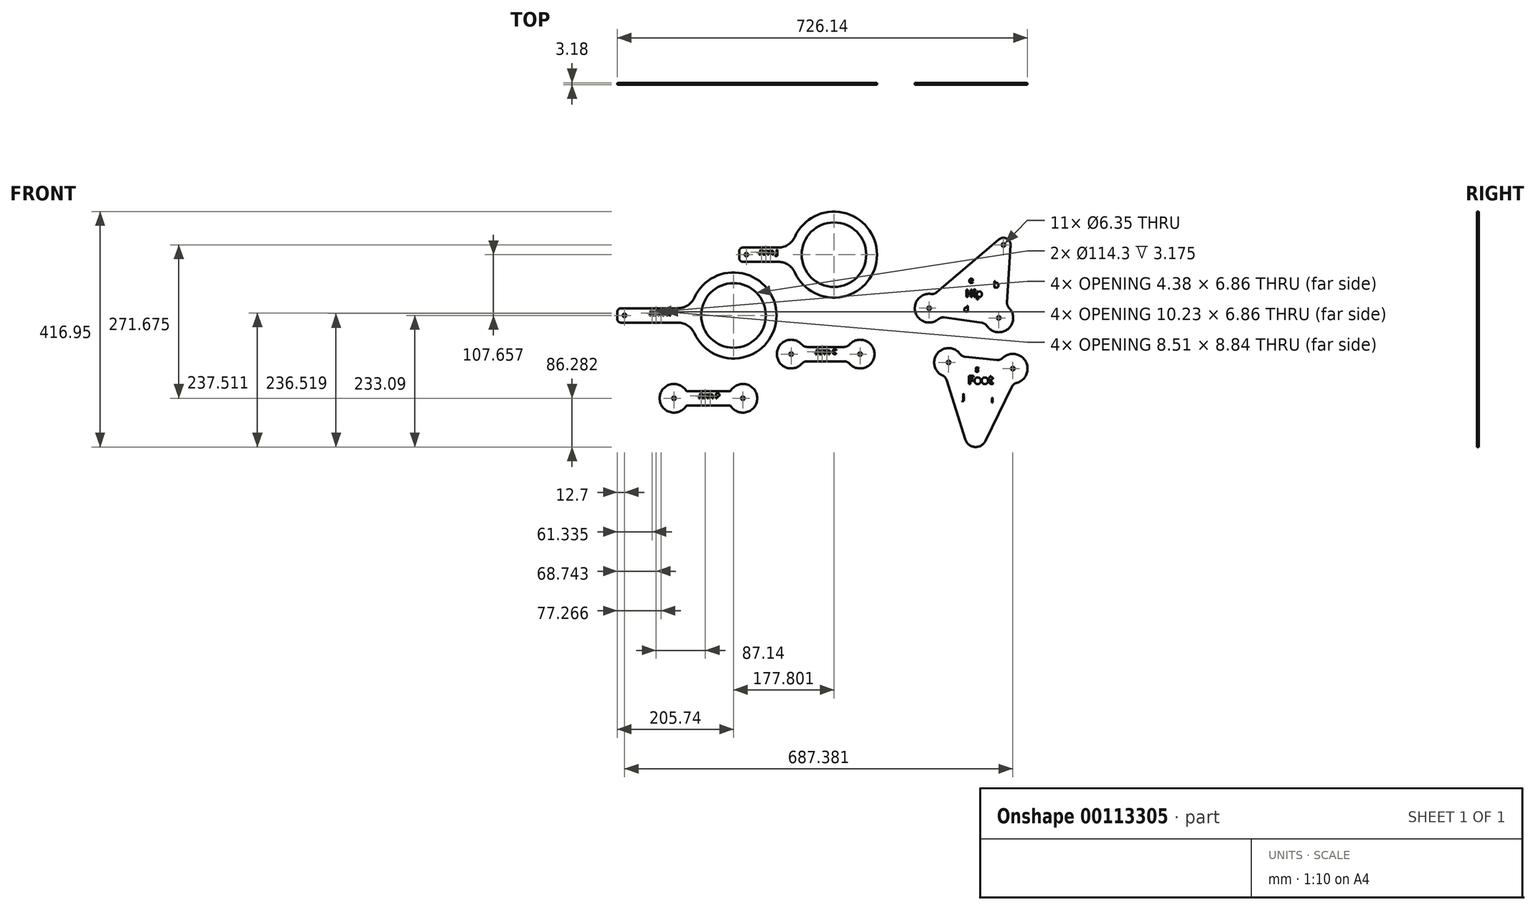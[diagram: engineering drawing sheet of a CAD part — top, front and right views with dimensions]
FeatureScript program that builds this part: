
annotation { "Feature Type Name" : "Feature", "Feature Type Description" : "" }
export const myFeature = defineFeature(function(context is Context, id is Id, definition is map)
    precondition{}
    {
        {
            var Q0;
            Q0=qCreatedBy(makeId("Front.planeOp"),FACE);
            var sketch = newSketch(context, id + "F0", { "sketchPlane" : qUnion([Q0])});
            skLineSegment(sketch, "E0", {"start": v(-141.12, 111.94) * mm, "end": v(13.82, 111.94) * mm, "construction": true});
            skLineSegment(sketch, "E1.bottom", {"start": v(-147.47, 124.64) * mm, "end": v(-84.55, 124.64) * mm});
            skLineSegment(sketch, "E1.top", {"start": v(-147.47, 99.24) * mm, "end": v(-84.55, 99.24) * mm});
            skLineSegment(sketch, "E1.left", {"start": v(-153.82, 118.29) * mm, "end": v(-153.82, 105.59) * mm});
            skCircle(sketch, "E2", {"center": v(-141.12, 111.94) * mm, "radius": 3.18 * mm});
            skPoint(sketch, "E3.visualSharp", {"position": v(-153.82, 124.64) * mm});
            skArc(sketch, "E3.filletArc", {"start": v(-147.47, 124.64) * mm, "mid": v(-151.96, 122.78) * mm, "end": v(-153.82, 118.29) * mm});
            skPoint(sketch, "E4.visualSharp", {"position": v(-153.82, 99.24) * mm});
            skArc(sketch, "E4.filletArc", {"start": v(-153.82, 105.59) * mm, "mid": v(-151.96, 101.1) * mm, "end": v(-147.47, 99.24) * mm});
            skText(sketch, "E5", { "text": "Arm J", "fontName": "OpenSans-Bold.ttf"});
            skArc(sketch, "E6", {"start": v(-55.62, 80.56) * mm, "mid": v(90.02, 111.94) * mm, "end": v(-55.62, 143.31) * mm});
            skCircle(sketch, "E7", {"center": v(13.82, 111.94) * mm, "radius": 57.15 * mm});
            skPoint(sketch, "E8.visualSharp", {"position": v(-61.31, 124.64) * mm});
            skArc(sketch, "E8.filletArc", {"start": v(-84.55, 124.64) * mm, "mid": v(-67.33, 129.71) * mm, "end": v(-55.62, 143.31) * mm});
            skPoint(sketch, "E9.visualSharp", {"position": v(-61.31, 99.24) * mm});
            skArc(sketch, "E9.filletArc", {"start": v(-55.62, 80.56) * mm, "mid": v(-67.33, 94.16) * mm, "end": v(-84.55, 99.24) * mm});
            const initialGuessF0  = {"E5": [-0.11858, 0.11194, 1, 0, 0.00888]};
            skSetInitialGuess(sketch, initialGuessF0);
            skSolve(sketch);
        }
        {
            var Q0;
            Q0=makeQuery(id+"F0.imprint","IMPRINT",FACE,{"disambiguationData":[TD([[makeQuery(id+"F0.imprint","IMPRINT",EDGE,{"derivedFrom":sQuery(id+"F0.wireOp",EDGE,"E1.bottom")}),-1.0]])]});
            extrude(context, id + "F1", {"entities" : qUnion([Q0]), "depth" : 3.17 * mm});
        }
        {
            var Q0;
            Q0=qCreatedBy(makeId("Front.planeOp"),FACE);
            var sketch = newSketch(context, id + "F2", { "sketchPlane" : qUnion([Q0])});
            skLineSegment(sketch, "E10", {"start": v(-357.02, 4.28) * mm, "end": v(-163.98, 4.28) * mm, "construction": true});
            skLineSegment(sketch, "E11.bottom", {"start": v(-363.37, 16.98) * mm, "end": v(-262.35, 16.98) * mm});
            skLineSegment(sketch, "E11.top", {"start": v(-363.37, -8.42) * mm, "end": v(-262.35, -8.42) * mm});
            skLineSegment(sketch, "E11.left", {"start": v(-369.72, 10.63) * mm, "end": v(-369.72, -2.07) * mm});
            skCircle(sketch, "E12", {"center": v(-357.02, 4.28) * mm, "radius": 3.18 * mm});
            skPoint(sketch, "E13.visualSharp", {"position": v(-369.72, 16.98) * mm});
            skArc(sketch, "E13.filletArc", {"start": v(-363.37, 16.98) * mm, "mid": v(-367.86, 15.12) * mm, "end": v(-369.72, 10.63) * mm});
            skPoint(sketch, "E14.visualSharp", {"position": v(-369.72, -8.42) * mm});
            skArc(sketch, "E14.filletArc", {"start": v(-369.72, -2.07) * mm, "mid": v(-367.86, -6.56) * mm, "end": v(-363.37, -8.42) * mm});
            skText(sketch, "E15", { "text": "Arm K", "fontName": "OpenSans-Bold.ttf"});
            skArc(sketch, "E16", {"start": v(-233.42, -27.1) * mm, "mid": v(-87.78, 4.28) * mm, "end": v(-233.42, 35.66) * mm});
            skCircle(sketch, "E17", {"center": v(-163.98, 4.28) * mm, "radius": 57.15 * mm});
            skPoint(sketch, "E18.visualSharp", {"position": v(-239.11, 16.98) * mm});
            skArc(sketch, "E18.filletArc", {"start": v(-262.35, 16.98) * mm, "mid": v(-245.13, 22.05) * mm, "end": v(-233.42, 35.66) * mm});
            skPoint(sketch, "E19.visualSharp", {"position": v(-239.11, -8.42) * mm});
            skArc(sketch, "E19.filletArc", {"start": v(-233.42, -27.1) * mm, "mid": v(-245.13, -13.5) * mm, "end": v(-262.35, -8.42) * mm});
            const initialGuessF2  = {"E15": [-0.31264, 0.00428, 1, 0, 0.00888]};
            skSetInitialGuess(sketch, initialGuessF2);
            skSolve(sketch);
        }
        {
            var Q0;
            Q0=makeQuery(id+"F2.imprint","IMPRINT",FACE,{"disambiguationData":[TD([[makeQuery(id+"F2.imprint","IMPRINT",EDGE,{"derivedFrom":sQuery(id+"F2.wireOp",EDGE,"E11.bottom")}),-1.0]])]});
            extrude(context, id + "F3", {"entities" : qUnion([Q0]), "depth" : 3.17 * mm});
        }
        {
            var Q0;
            Q0=qCreatedBy(makeId("Front.planeOp"),FACE);
            var sketch = newSketch(context, id + "F4", { "sketchPlane" : qUnion([Q0])});
            skLineSegment(sketch, "E20", {"start": v(-61.9, -64.2) * mm, "end": v(60.02, -64.2) * mm, "construction": true});
            skLineSegment(sketch, "E21.bottom", {"start": v(-33.5, -51.5) * mm, "end": v(31.62, -51.5) * mm});
            skLineSegment(sketch, "E21.top", {"start": v(-33.5, -76.9) * mm, "end": v(31.62, -76.9) * mm});
            skCircle(sketch, "E22", {"center": v(-61.9, -64.2) * mm, "radius": 3.18 * mm});
            skCircle(sketch, "E23", {"center": v(60.02, -64.2) * mm, "radius": 3.18 * mm});
            skPoint(sketch, "E24.visualSharp", {"position": v(110.82, -76.9) * mm});
            skText(sketch, "E25", { "text": "Arm C", "fontName": "OpenSans-Bold.ttf"});
            skArc(sketch, "E26", {"start": v(41.08, -81.14) * mm, "mid": v(85.42, -64.2) * mm, "end": v(41.08, -47.27) * mm});
            skPoint(sketch, "E27.visualSharp", {"position": v(38.02, -51.5) * mm});
            skArc(sketch, "E27.filletArc", {"start": v(31.62, -51.5) * mm, "mid": v(36.8, -50.4) * mm, "end": v(41.08, -47.27) * mm});
            skPoint(sketch, "E28.visualSharp", {"position": v(38.02, -76.9) * mm});
            skArc(sketch, "E28.filletArc", {"start": v(41.08, -81.14) * mm, "mid": v(36.8, -78.01) * mm, "end": v(31.62, -76.9) * mm});
            skArc(sketch, "E29", {"start": v(-42.97, -47.27) * mm, "mid": v(-87.3, -64.2) * mm, "end": v(-42.97, -81.14) * mm});
            skPoint(sketch, "E30.visualSharp", {"position": v(-39.9, -51.5) * mm});
            skArc(sketch, "E30.filletArc", {"start": v(-42.97, -47.27) * mm, "mid": v(-38.7, -50.4) * mm, "end": v(-33.5, -51.5) * mm});
            skPoint(sketch, "E31.visualSharp", {"position": v(-39.9, -76.9) * mm});
            skArc(sketch, "E31.filletArc", {"start": v(-33.5, -76.9) * mm, "mid": v(-38.7, -78.01) * mm, "end": v(-42.97, -81.14) * mm});
            const initialGuessF4  = {"E25": [-0.01884, -0.0642, 1, 0, 0.00888]};
            skSetInitialGuess(sketch, initialGuessF4);
            skSolve(sketch);
        }
        {
            var Q0;
            Q0=makeQuery(id+"F4.imprint","IMPRINT",FACE,{"disambiguationData":[TD([[makeQuery(id+"F4.imprint","IMPRINT",EDGE,{"derivedFrom":sQuery(id+"F4.wireOp",EDGE,"E21.bottom")}),-1.0]])]});
            extrude(context, id + "F5", {"entities" : qUnion([Q0]), "depth" : 3.17 * mm});
        }
        {
            var Q0;
            Q0=qCreatedBy(makeId("Front.planeOp"),FACE);
            var sketch = newSketch(context, id + "F6", { "sketchPlane" : qUnion([Q0])});
            skLineSegment(sketch, "E32", {"start": v(-269.35, -142.53) * mm, "end": v(-147.43, -142.53) * mm, "construction": true});
            skLineSegment(sketch, "E33.bottom", {"start": v(-247.35, -129.83) * mm, "end": v(-169.42, -129.83) * mm});
            skLineSegment(sketch, "E33.top", {"start": v(-247.35, -155.23) * mm, "end": v(-169.42, -155.23) * mm});
            skCircle(sketch, "E34", {"center": v(-269.35, -142.53) * mm, "radius": 3.18 * mm});
            skCircle(sketch, "E35", {"center": v(-147.43, -142.53) * mm, "radius": 3.18 * mm});
            skText(sketch, "E36", { "text": "Arm P\n", "fontName": "OpenSans-Bold.ttf"});
            skArc(sketch, "E37", {"start": v(-169.42, -155.23) * mm, "mid": v(-122.03, -142.53) * mm, "end": v(-169.42, -129.83) * mm});
            skArc(sketch, "E38", {"start": v(-247.35, -129.83) * mm, "mid": v(-294.75, -142.53) * mm, "end": v(-247.35, -155.23) * mm});
            const initialGuessF6  = {"E36": [-0.2255, -0.14253, 1, 0, 0.00888]};
            skSetInitialGuess(sketch, initialGuessF6);
            skSolve(sketch);
        }
        {
            var Q0;
            Q0=makeQuery(id+"F6.imprint","IMPRINT",FACE,{"disambiguationData":[TD([[makeQuery(id+"F6.imprint","IMPRINT",EDGE,{"derivedFrom":sQuery(id+"F6.wireOp",EDGE,"E33.bottom")}),-1.0]])]});
            extrude(context, id + "F7", {"entities" : qUnion([Q0]), "depth" : 3.17 * mm});
        }
        {
            var Q0;
            Q0=qCreatedBy(makeId("Front.planeOp"),FACE);
            var sketch = newSketch(context, id + "F8", { "sketchPlane" : qUnion([Q0])});
            skLineSegment(sketch, "E39", {"start": v(182.27, 17.12) * mm, "end": v(313.74, 129.15) * mm, "construction": true});
            skLineSegment(sketch, "E40", {"start": v(313.74, 129.15) * mm, "end": v(305.53, -0.13) * mm, "construction": true});
            skLineSegment(sketch, "E41", {"start": v(305.53, -0.13) * mm, "end": v(182.27, 17.12) * mm, "construction": true});
            skText(sketch, "E42", { "text": "b", "fontName": "OpenSans-Regular.ttf"});
            skText(sketch, "E43", { "text": "e", "fontName": "OpenSans-Regular.ttf"});
            skText(sketch, "E44", { "text": "d", "fontName": "OpenSans-Regular.ttf"});
            skText(sketch, "E45", { "text": "Hip", "fontName": "OpenSans-Bold.ttf"});
            skPoint(sketch, "E46", {"position": v(243.9, 8.5) * mm});
            skCircle(sketch, "E47", {"center": v(182.27, 17.12) * mm, "radius": 3.18 * mm});
            skCircle(sketch, "E48", {"center": v(305.53, -0.13) * mm, "radius": 3.18 * mm});
            skCircle(sketch, "E49", {"center": v(313.74, 129.15) * mm, "radius": 3.18 * mm});
            skLineSegment(sketch, "E50.0", {"start": v(275.65, -8.77) * mm, "end": v(208.64, 0.6) * mm});
            skLineSegment(sketch, "E50.1", {"start": v(326.41, 128.34) * mm, "end": v(320, 27.4) * mm});
            skLineSegment(sketch, "E50.2", {"start": v(195.65, 45.2) * mm, "end": v(305.5, 138.81) * mm});
            skPoint(sketch, "E51.visualSharp", {"position": v(328.3, 158.25) * mm});
            skArc(sketch, "E51.filletArc", {"start": v(326.41, 128.34) * mm, "mid": v(319.42, 140.5) * mm, "end": v(305.5, 138.81) * mm});
            skArc(sketch, "E52", {"start": v(185.7, 42.3) * mm, "mid": v(157.89, 10.02) * mm, "end": v(198.67, -2.27) * mm});
            skArc(sketch, "E53", {"start": v(284.43, -14.28) * mm, "mid": v(321.58, -19.82) * mm, "end": v(323.63, 17.69) * mm});
            skPoint(sketch, "E54.visualSharp", {"position": v(319.6, 21.02) * mm});
            skArc(sketch, "E54.filletArc", {"start": v(320, 27.4) * mm, "mid": v(320.78, 22.16) * mm, "end": v(323.63, 17.69) * mm});
            skPoint(sketch, "E55.visualSharp", {"position": v(281.99, -9.66) * mm});
            skArc(sketch, "E55.filletArc", {"start": v(284.43, -14.28) * mm, "mid": v(280.63, -10.59) * mm, "end": v(275.65, -8.77) * mm});
            skPoint(sketch, "E56.visualSharp", {"position": v(202.3, 1.5) * mm});
            skArc(sketch, "E56.filletArc", {"start": v(208.64, 0.6) * mm, "mid": v(203.35, 0.23) * mm, "end": v(198.67, -2.27) * mm});
            skPoint(sketch, "E57.visualSharp", {"position": v(190.78, 41.06) * mm});
            skArc(sketch, "E57.filletArc", {"start": v(185.7, 42.3) * mm, "mid": v(190.99, 42.69) * mm, "end": v(195.65, 45.2) * mm});
            const initialGuessF8  = {"E42": [0.2966, 0.05383, 1, 0, 0.01078], "E43": [0.25258, 0.0617, 1, 0, 0.01017], "E44": [0.2439, 0.01126, 1, 0, 0.00937], "E45": [0.24654, 0.03705, 1, 0, 0.01256]};
            skSetInitialGuess(sketch, initialGuessF8);
            skSolve(sketch);
        }
        {
            var Q0;
            Q0=makeQuery(id+"F8.imprint","IMPRINT",FACE,{"disambiguationData":[TD([[makeQuery(id+"F8.imprint","IMPRINT",EDGE,{"derivedFrom":sQuery(id+"F8.wireOp",EDGE,"E42.sketch_text.stroke-0")}),1.0]])]});
            extrude(context, id + "F9", {"entities" : qUnion([Q0]), "depth" : 3.17 * mm});
        }
        {
            var Q0;
            Q0=qCreatedBy(makeId("Front.planeOp"),FACE);
            var sketch = newSketch(context, id + "F10", { "sketchPlane" : qUnion([Q0])});
            skLineSegment(sketch, "E58", {"start": v(216.59, -79.04) * mm, "end": v(330.36, -89.96) * mm, "construction": true});
            skLineSegment(sketch, "E59", {"start": v(330.36, -89.96) * mm, "end": v(263.24, -226.79) * mm, "construction": true});
            skLineSegment(sketch, "E60", {"start": v(263.24, -226.79) * mm, "end": v(216.59, -79.04) * mm, "construction": true});
            skText(sketch, "E61", { "text": "g\n", "fontName": "OpenSans-Regular.ttf"});
            skText(sketch, "E62", { "text": "i\n", "fontName": "OpenSans-Regular.ttf"});
            skText(sketch, "E63", { "text": "j\n", "fontName": "OpenSans-Regular.ttf"});
            skCircle(sketch, "E64", {"center": v(216.59, -79.04) * mm, "radius": 3.18 * mm});
            skCircle(sketch, "E65", {"center": v(330.36, -89.96) * mm, "radius": 3.18 * mm});
            skText(sketch, "E66", { "text": "Foot", "fontName": "OpenSans-Bold.ttf"});
            skLineSegment(sketch, "E67.0", {"start": v(246.07, -69.1) * mm, "end": v(302.44, -74.52) * mm});
            skLineSegment(sketch, "E67.1", {"start": v(246.35, -215.5) * mm, "end": v(213.03, -109.94) * mm});
            skLineSegment(sketch, "E67.2", {"start": v(328.87, -121.84) * mm, "end": v(281.62, -218.15) * mm});
            skPoint(sketch, "E68.visualSharp", {"position": v(260.67, -260.85) * mm});
            skArc(sketch, "E68.filletArc", {"start": v(246.35, -215.5) * mm, "mid": v(263.1, -228.75) * mm, "end": v(281.62, -218.15) * mm});
            skArc(sketch, "E69", {"start": v(237.05, -64) * mm, "mid": v(196.84, -63.06) * mm, "end": v(206.14, -102.19) * mm});
            skArc(sketch, "E70", {"start": v(337.02, -115.15) * mm, "mid": v(353.1, -77.26) * mm, "end": v(312.4, -71.08) * mm});
            skPoint(sketch, "E71.visualSharp", {"position": v(239.7, -68.5) * mm});
            skArc(sketch, "E71.filletArc", {"start": v(237.05, -64) * mm, "mid": v(241.01, -67.51) * mm, "end": v(246.07, -69.1) * mm});
            skPoint(sketch, "E72.visualSharp", {"position": v(308.93, -75.15) * mm});
            skArc(sketch, "E72.filletArc", {"start": v(302.44, -74.52) * mm, "mid": v(307.8, -73.89) * mm, "end": v(312.4, -71.08) * mm});
            skPoint(sketch, "E73.visualSharp", {"position": v(331.74, -115.98) * mm});
            skArc(sketch, "E73.filletArc", {"start": v(337.02, -115.15) * mm, "mid": v(332.22, -117.6) * mm, "end": v(328.87, -121.84) * mm});
            skPoint(sketch, "E74.visualSharp", {"position": v(211.1, -103.84) * mm});
            skArc(sketch, "E74.filletArc", {"start": v(213.03, -109.94) * mm, "mid": v(210.4, -105.33) * mm, "end": v(206.14, -102.19) * mm});
            const initialGuessF10  = {"E61": [0.2643, -0.0932, 1, 0, 0.00715], "E62": [0.2926, -0.15022, 1, 0, 0.00817], "E63": [0.24125, -0.14474, 1, 0, 0.00953], "E66": [0.25052, -0.11701, 1, 0, 0.01478]};
            skSetInitialGuess(sketch, initialGuessF10);
            skSolve(sketch);
        }
        {
            var Q0;
            Q0=makeQuery(id+"F10.imprint","IMPRINT",FACE,{"disambiguationData":[TD([[makeQuery(id+"F10.imprint","IMPRINT",EDGE,{"derivedFrom":sQuery(id+"F10.wireOp",EDGE,"E61.sketch_text.stroke-0")}),1.0]])]});
            extrude(context, id + "F11", {"entities" : qUnion([Q0]), "depth" : 3.17 * mm});
        }
    });
